# Revit family: Ytong sestava plochých překladů
name_source: partatom
category: Generic Models
units: mm (PartAtom-declared; Revit-internal decimal feet)

## family parameters
Always vertical = Yes
Can host rebar = No
Cut with Voids When Loaded = No
Part Type = Normal
Room Calculation Point = No
Round Connector Dimension = Use Diameter
Shared = Yes
Work Plane-Based = No

## types (1)
- Ytong sestava plochých překladů
    Autor = BIM Technology s.r.o.
    Description = Pórobetonové prvky vyztužené betonářskou výztuží
    Hláška při nenalezení = Překročena maximální světlost otvoru!
    IfcExportAs = IfcBeam
    IfcExportType = LINTEL
    Krátký popis = Pórobetonové prvky vyztužené betonářskou výztuží
    Manufacturer = Ytong
    Materiál = pórobeton AAC 4,5-600
    Minimální délka nosníku = 1250 mm  [stored 4.10105 ft]
    Nevalidní šířka = 50 mm  [stored 0.164042 ft]
    Název tabulky = Ytong sestava plochých překladů
    Odkaz na DoP = https://storefrontapi.commerce.xella.com
    Odkaz na stavební postup = https://storefrontapi.commerce.xella.com
    Odkaz na technický list = https://storefrontapi.commerce.xella.com
    Odkaz na web = https://www.xella.cz
    Skupina prvků = Překlad
    URL = https://www.xella.cz
    Zobrazit ve výkazech = Yes

note: [stored X ft] marks values corroborated as IEEE doubles in the binary element streams (Revit-internal decimal feet)
